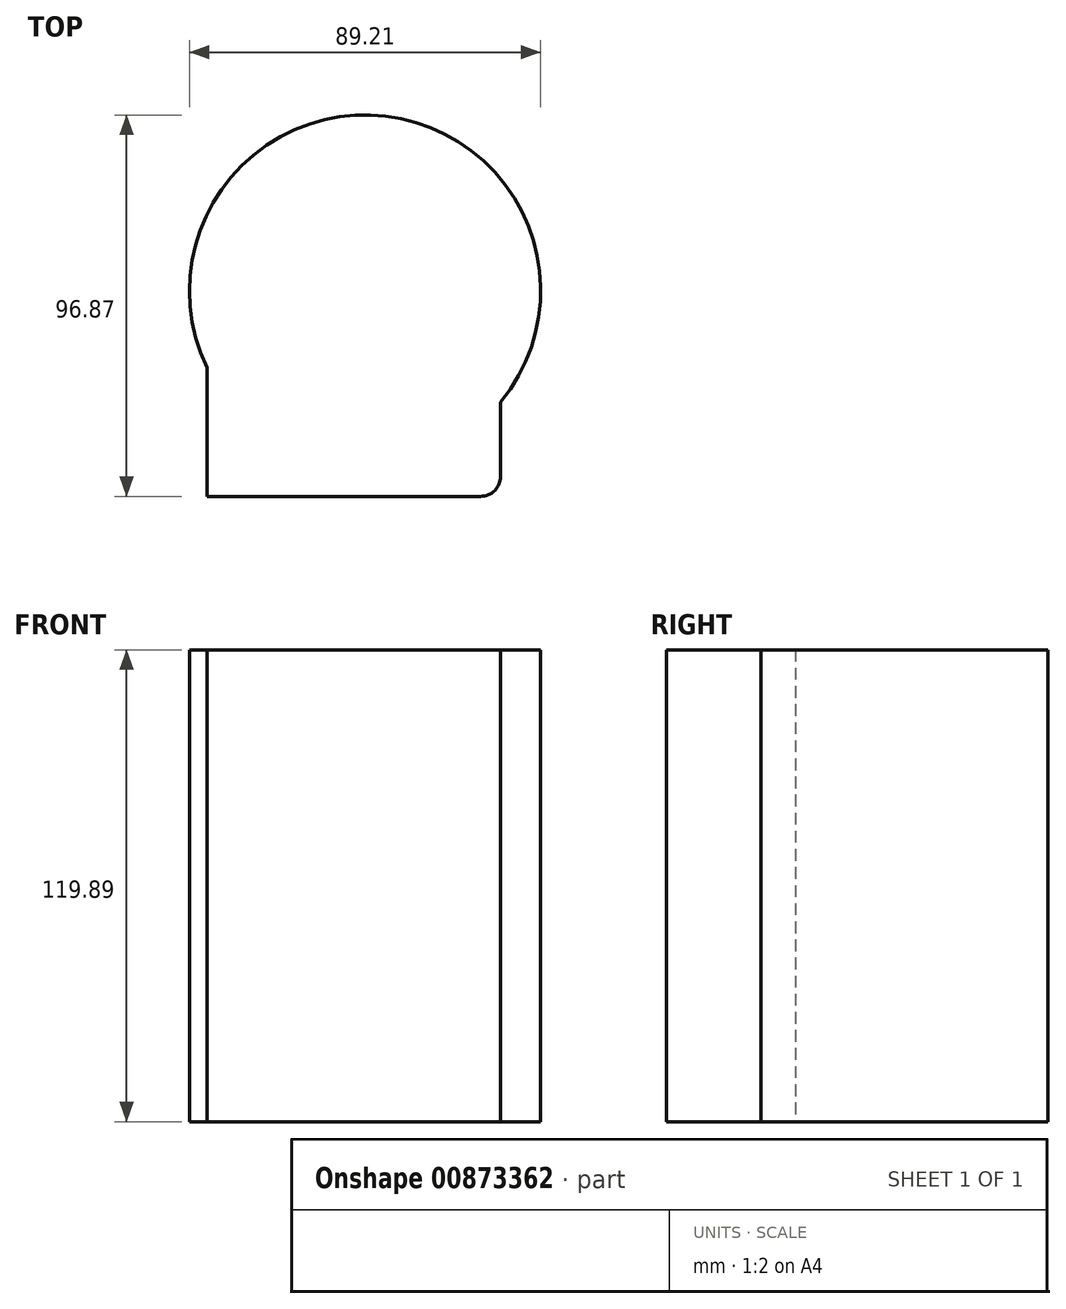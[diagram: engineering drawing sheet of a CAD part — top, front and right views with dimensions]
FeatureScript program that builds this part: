
annotation { "Feature Type Name" : "Feature", "Feature Type Description" : "" }
export const myFeature = defineFeature(function(context is Context, id is Id, definition is map)
    precondition{}
    {
        {
            var Q0;
            Q0=qCreatedBy(makeId("Top.planeOp"),FACE);
            var sketch = newSketch(context, id + "F0", { "sketchPlane" : qUnion([Q0])});
            skLineSegment(sketch, "E0.bottom", {"start": v(0, 0) * mm, "end": v(74.54, 0) * mm});
            skLineSegment(sketch, "E0.top", {"start": v(0, -52.26) * mm, "end": v(74.54, -52.26) * mm});
            skLineSegment(sketch, "E0.left", {"start": v(0, 0) * mm, "end": v(0, -52.26) * mm});
            skLineSegment(sketch, "E0.right", {"start": v(74.54, 0) * mm, "end": v(74.54, -52.26) * mm});
            skCircle(sketch, "E1", {"center": v(40.1, 0) * mm, "radius": 44.6 * mm});
            skSolve(sketch);
        }
        {
            var Q0;
            {var subQ0=sQuery(id+"F0.wireOp",EDGE,"E0.bottom");Q0=makeQuery(id+"F0.imprint","IMPRINT",FACE,{"disambiguationData":[TD([[makeQuery(id+"F0.imprint","IMPRINT",EDGE,{"derivedFrom":subQ0}),1.0]])]});}
            var Q1;
            {var subQ0=sQuery(id+"F0.wireOp",EDGE,"E0.bottom");Q1=makeQuery(id+"F0.imprint","IMPRINT",FACE,{"disambiguationData":[TD([[makeQuery(id+"F0.imprint","IMPRINT",EDGE,{"derivedFrom":subQ0}),-1.0]])]});}
            var Q2;
            {var subQ0=sQuery(id+"F0.wireOp",EDGE,"E0.top");Q2=makeQuery(id+"F0.imprint","IMPRINT",FACE,{"disambiguationData":[TD([[makeQuery(id+"F0.imprint","IMPRINT",EDGE,{"derivedFrom":subQ0}),1.0]])]});}
            extrude(context, id + "F1", {"entities" : qUnion([Q0, Q1, Q2]), "depth" : 119.89 * mm, "offsetDistance" : 25.4 * mm});
        }
        {
            var Q0;
            Q0=makeQuery(id+"F1.opExtrude","SWEPT_EDGE",EDGE,{"disambiguationData":[OSD([sQuery(id+"F0.wireOp",EDGE,"E0.top"),sQuery(id+"F0.wireOp",EDGE,"E0.right")])]});
            fillet(context, id + "F2", {"entities" : qUnion([Q0]), "radius" : 5.08 * mm, "tangentPropagation" : true, "allowEdgeOverflow" : false});
        }
    });
